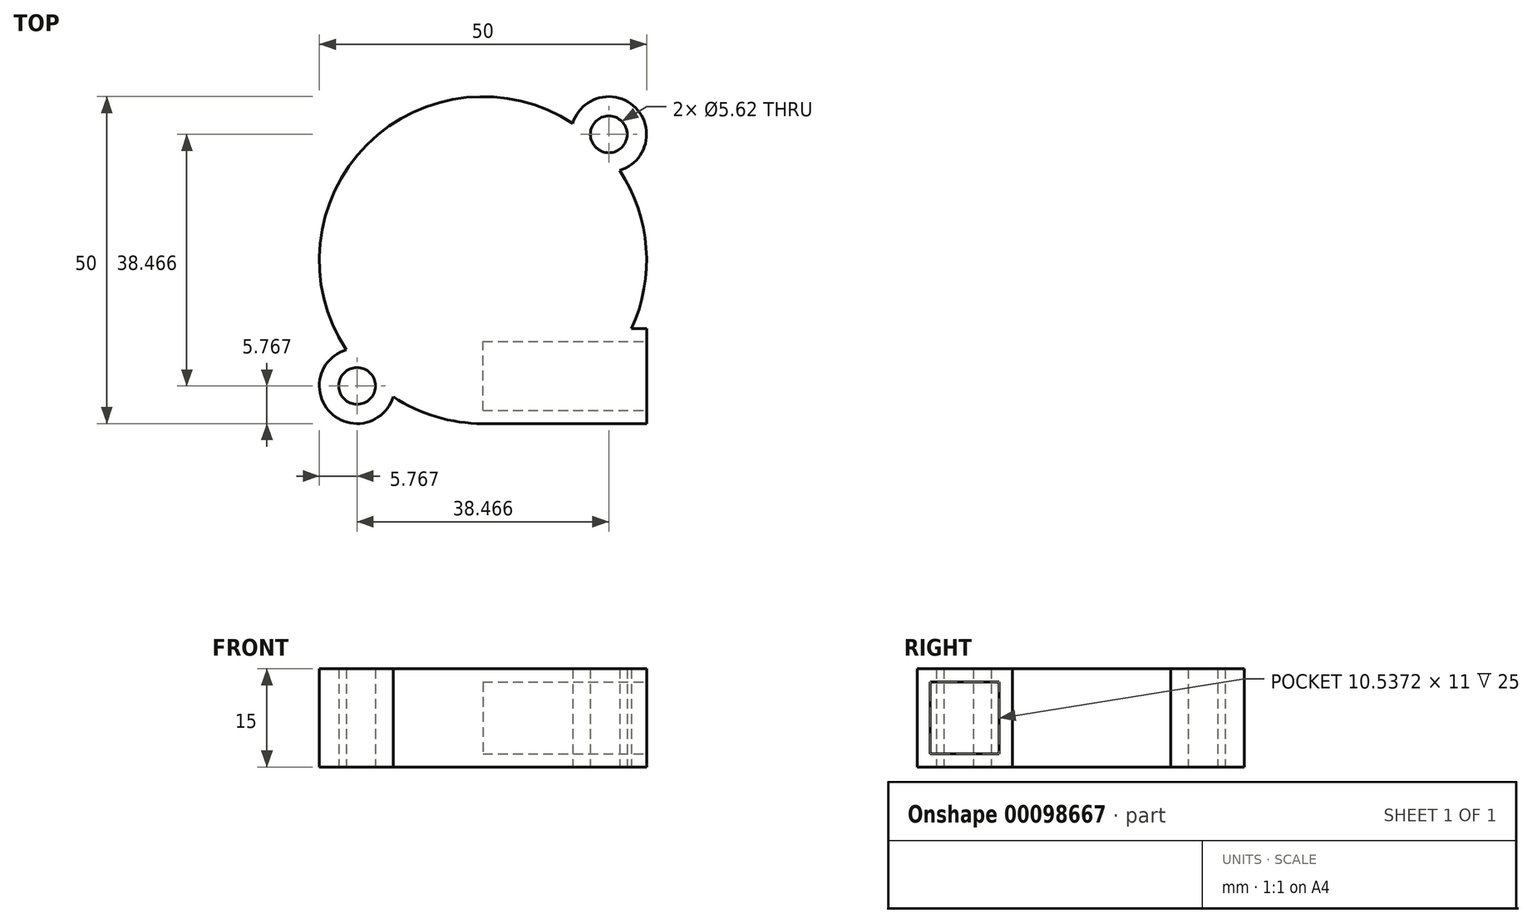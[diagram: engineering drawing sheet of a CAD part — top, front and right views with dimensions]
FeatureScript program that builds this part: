
annotation { "Feature Type Name" : "Feature", "Feature Type Description" : "" }
export const myFeature = defineFeature(function(context is Context, id is Id, definition is map)
    precondition{}
    {
        {
            var Q0;
            Q0=qCreatedBy(makeId("Top.planeOp"),FACE);
            var sketch = newSketch(context, id + "F0", { "sketchPlane" : qUnion([Q0])});
            skLineSegment(sketch, "E0.bottom", {"start": v(25, 0) * mm, "end": v(50, 0) * mm});
            skLineSegment(sketch, "E0.right", {"start": v(50, 0) * mm, "end": v(50, 14.54) * mm});
            skLineSegment(sketch, "E1", {"start": v(25, 50) * mm, "end": v(25, 0) * mm, "construction": true});
            skCircle(sketch, "E2", {"center": v(44.23, 44.23) * mm, "radius": 2.8 * mm});
            skLineSegment(sketch, "E3", {"start": v(0, 50) * mm, "end": v(50, 0) * mm, "construction": true});
            skCircle(sketch, "E4.MirrorC", {"center": v(5.77, 5.77) * mm, "radius": 2.8 * mm});
            skArc(sketch, "E5", {"start": v(38.71, 45.9) * mm, "mid": v(7.32, 42.68) * mm, "end": v(4.1, 11.29) * mm});
            skArc(sketch, "E6", {"start": v(45.9, 38.71) * mm, "mid": v(48.31, 48.31) * mm, "end": v(38.71, 45.9) * mm});
            skArc(sketch, "E7.MirrorCS", {"start": v(11.29, 4.1) * mm, "mid": v(1.69, 1.69) * mm, "end": v(4.1, 11.29) * mm});
            skArc(sketch, "E8.trimOffspring", {"start": v(11.29, 4.1) * mm, "mid": v(42.68, 7.32) * mm, "end": v(45.9, 38.71) * mm});
            skPoint(sketch, "E9.orphan", {"position": v(0, 0) * mm});
            skPoint(sketch, "E10.orphan", {"position": v(50, 50) * mm});
            skLineSegment(sketch, "E11", {"start": v(50, 14.54) * mm, "end": v(47.7, 14.54) * mm});
            skSolve(sketch);
        }
        {
            var Q0;
            Q0=qSketchRegion(id+"F0",true);
            extrude(context, id + "F1", {"entities" : qUnion([Q0]), "depth" : 15 * mm});
        }
        {
            var Q0;
            Q0=makeQuery(id+"F1.opExtrude","SWEPT_FACE",FACE,{"disambiguationData":[OSD([sQuery(id+"F0.wireOp",EDGE,"E0.right")])]});
            var sketch = newSketch(context, id + "F2", { "sketchPlane" : qUnion([Q0])});
            skLineSegment(sketch, "E12.0", {"start": v(2, 2) * mm, "end": v(12.54, 2) * mm});
            skLineSegment(sketch, "E12.1", {"start": v(2, 13) * mm, "end": v(2, 2) * mm});
            skLineSegment(sketch, "E12.2", {"start": v(12.54, 13) * mm, "end": v(2, 13) * mm});
            skLineSegment(sketch, "E12.3", {"start": v(12.54, 2) * mm, "end": v(12.54, 13) * mm});
            skSolve(sketch);
        }
        {
            var Q0;
            Q0=qSketchRegion(id+"F2",true);
            extrude(context, id + "F3", {"entities" : qUnion([Q0]), "operationType" : NewBodyOperationType.REMOVE, "oppositeDirection" : true, "depth" : 25 * mm});
        }
    });
